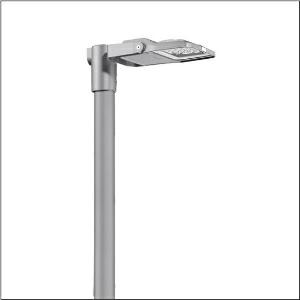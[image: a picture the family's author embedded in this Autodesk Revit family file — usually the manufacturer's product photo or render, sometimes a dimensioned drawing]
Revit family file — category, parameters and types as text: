
# Revit family: floodlight_fl_21_iq_micro___pl64_5xa7761a2e3a_b98d
name_source: partatom
category: Lighting Fixtures
units: mm (PartAtom-declared; Revit-internal decimal feet)

## family parameters
Cut with Voids When Loaded = No
Host = Face
Light Source = No
Part Type = Normal
Room Calculation Point = No
Round Connector Dimension = Use Diameter
Shared = No

## types (1)
- --- (1 x LED, 2870 lm, 23.1 W, 3000K)
    Apparent Load = 23 VA
    CIE Flux Codes = 28 80 98 100 100
    Color Rendering = 70
    Color Temperature = 3000K
    Default Elevation = 1800 mm
    Description = Floodlight FL 21 iQ micro, floodlight, primary light control with lens, of PMMA, primary optical cover: protective disc, of toughened safety glass, transparent, light distribution: PL64, light emission: direct distribution, installation type: surface-mounted, LED, High Power LED, rated luminous flux: 2.870lm, luminous efficacy: 124lm/W, light colour: 730, colour temperature: 3000K, control: optimised constant luminous flux control (CLO 2.0), Desk-Remote (wireless, voltage-free reading and setting of iQ features in the workshop via application-optimized NFC function/RFID function), Light-Fading, Smart-Wire, Night-Set, Lumen-Switch, Temp-Guard, Auto-Match, with terminal, 6-pole, mains connection: 220..240V, AC, 50/60Hz, start of lifetime: 23W, end of service life: 24W, reduction: 11W, luminaire housing, of diecast aluminium, powder-coated, Siteco® metallic grey (DB 702S), corrosivity category C5 mid according to DIN EN ISO 12944, sealing non-destructively replaceable, please order mast flange separately, mast bracket, of steel, galvanised, powder-coated, Siteco® metallic grey (DB 702S), protection rating (complete): IP66, insulation class (complete): insulation class II (safety insulation), certification: CE, ENEC, VDE, protection symbol: D, impact resistance: IK07, permissible operating ambient temperature: -40..+40°C, permissible operating ambient temperature for outdoor applications: -40..+50°C, standard: DIN EN 12944, LABS conformity tested according to VDMA 24364:2018-05, packaging unit: 1 piece

Light Distribution: PL64
    Height = 65 mm
    Lamp = 1 x LED
    Lamp Light Flux = 2870 lm
    Lamp Power = 23.1 W
    Lamp count = 1
    Length = 312 mm
    Luminous efficacy = 124 lm/W
    Manufacturer = Siteco
    ModVariant = No
    Model = 5XA7761A2E3A
    Number of Poles = 1
    OnlyDefault = Yes
    Power Factor = 1
    Product Name = Floodlight FL 21 iQ micro | PL64
    Product group = floodlight | pylon top
    ProductGroupID = 6101
    Protection Class = Protection class II
    Protection Degree = IP 66
    RLX_Detail_Level = 1
    RLX_Emergency_Light_Flux = 0 lm
    RLX_Emergency_Type = 0
    RLX_Emergency_Type_DB = No
    RlxData = <blob elided: 101773 chars, md5=cc7015e1>
    Socket = socket
    Standby Power = 0 W
    System Light Flux = 2870 lm
    System Power = 23 W
    Type Comments = factory setting: luminous flux: 100 % | dim-lin: 254 | 455 mA
    Type Image = l_1007121.jpg
    URL = http://relux.com
    VarID = @adj_132267
    Voltage = 0 V
    Weight = 0.00 kg
    Width = 230 mm

## geometry (parser evidence)
native form markers: Blend x4, Sweep x11
no freeform markers — native parametric forms only
